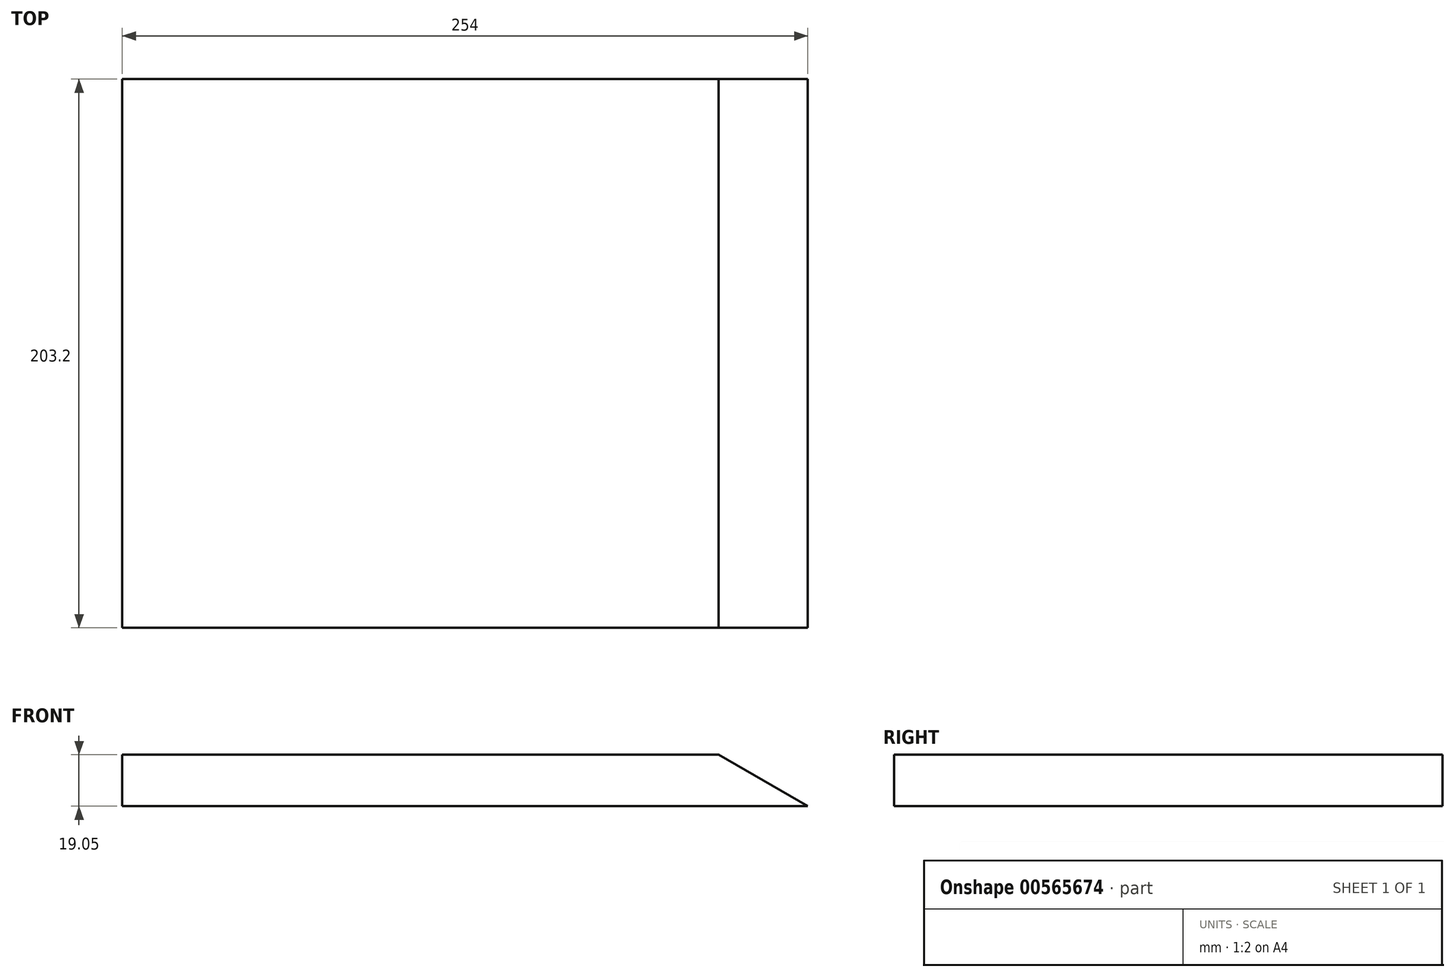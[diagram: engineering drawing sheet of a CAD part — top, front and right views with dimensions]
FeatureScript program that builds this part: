
annotation { "Feature Type Name" : "Feature", "Feature Type Description" : "" }
export const myFeature = defineFeature(function(context is Context, id is Id, definition is map)
    precondition{}
    {
        {
            var Q0;
            Q0=qCreatedBy(makeId("Front.planeOp"),FACE);
            var sketch = newSketch(context, id + "F0", { "sketchPlane" : qUnion([Q0])});
            skLineSegment(sketch, "E0", {"start": v(-115.84, 57.33) * mm, "end": v(-115.84, 38.28) * mm});
            skLineSegment(sketch, "E1", {"start": v(-115.84, 38.28) * mm, "end": v(138.16, 38.28) * mm});
            skLineSegment(sketch, "E2", {"start": v(138.16, 38.28) * mm, "end": v(105.16, 57.33) * mm});
            skLineSegment(sketch, "E3", {"start": v(105.16, 57.33) * mm, "end": v(-115.84, 57.33) * mm});
            skSolve(sketch);
        }
        {
            var Q0;
            Q0=makeQuery(id+"F0.imprint","IMPRINT",FACE,{"disambiguationData":[TD([[makeQuery(id+"F0.imprint","IMPRINT",EDGE,{"derivedFrom":sQuery(id+"F0.wireOp",EDGE,"E0")}),1.0]])]});
            extrude(context, id + "F1", {"entities" : qUnion([Q0]), "depth" : 203.2 * mm, "offsetDistance" : 25.4 * mm});
        }
    });
